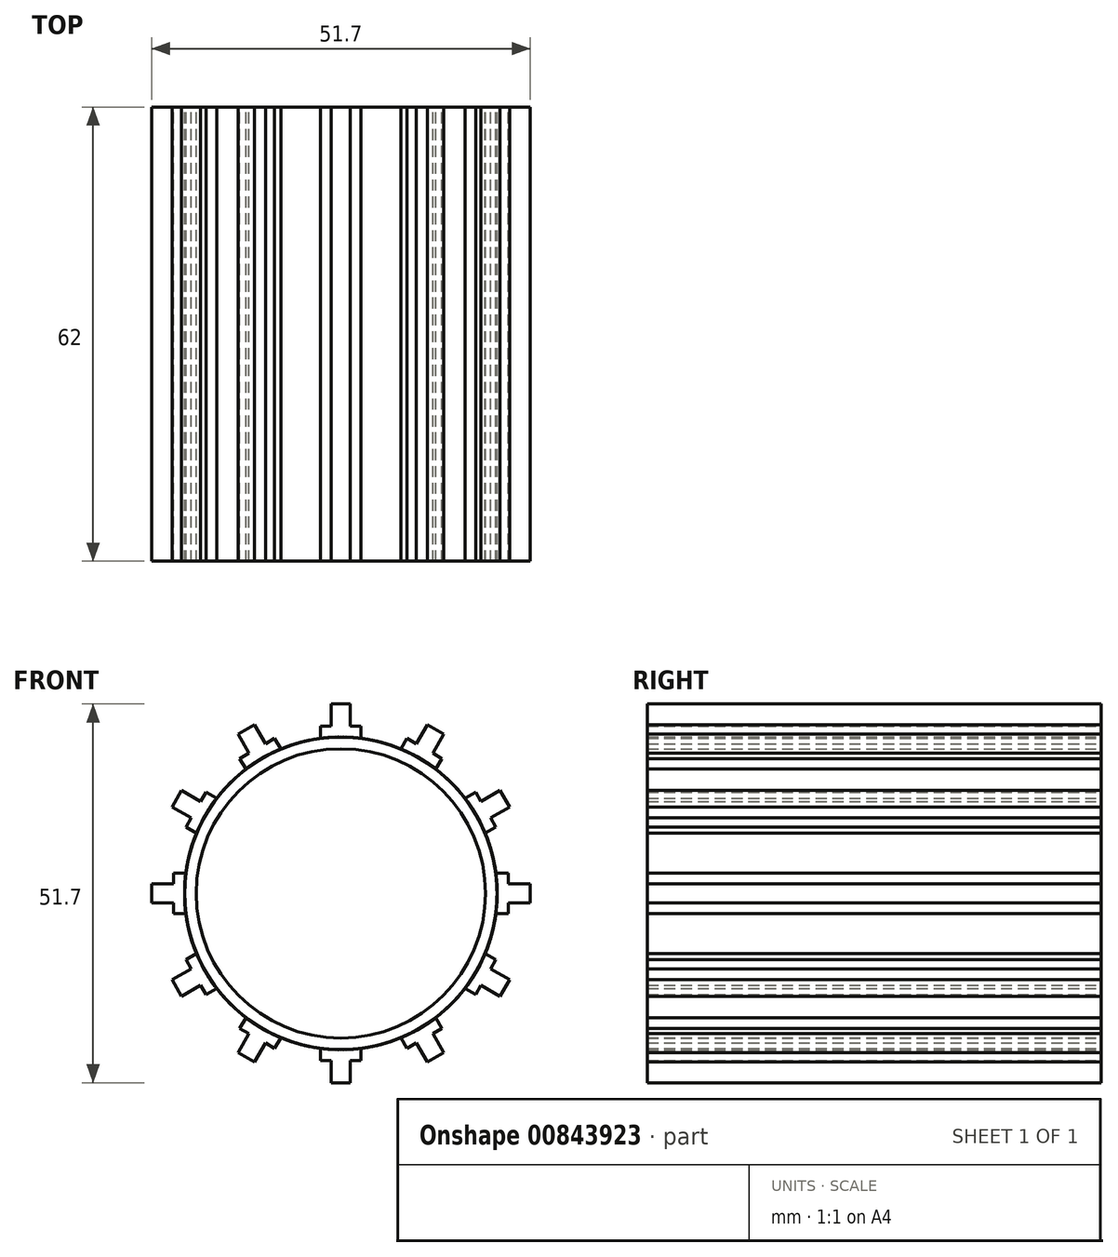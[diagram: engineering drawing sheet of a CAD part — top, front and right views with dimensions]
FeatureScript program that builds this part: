
annotation { "Feature Type Name" : "Feature", "Feature Type Description" : "" }
export const myFeature = defineFeature(function(context is Context, id is Id, definition is map)
    precondition{}
    {
        {
            var Q0;
            Q0=qCreatedBy(makeId("Front.planeOp"),FACE);
            var sketch = newSketch(context, id + "F0", { "sketchPlane" : qUnion([Q0])});
            skCircle(sketch, "E0", {"center": v(0, 0) * mm, "radius": 19.75 * mm});
            skCircle(sketch, "E1.0", {"center": v(0, 0) * mm, "radius": 21.35 * mm});
            skSolve(sketch);
        }
        {
            var Q0;
            Q0=makeQuery(id+"F0.imprint","IMPRINT",FACE,{"disambiguationData":[TD([[makeQuery(id+"F0.imprint","IMPRINT",EDGE,{"derivedFrom":sQuery(id+"F0.wireOp",EDGE,"E0")}),-1.0]])]});
            extrude(context, id + "F1", {"entities" : qUnion([Q0]), "depth" : 62 * mm, "offsetDistance" : 25 * mm});
        }
        {
            var Q0;
            Q0=makeQuery(id+"F1.opExtrude","CAP_FACE",FACE,{"disambiguationData":[OSD([sQuery(id+"F0.wireOp",EDGE,"E0"),sQuery(id+"F0.wireOp",EDGE,"E1.0")])],"isStart":true});
            var sketch = newSketch(context, id + "F2", { "sketchPlane" : qUnion([Q0])});
            skLineSegment(sketch, "E2", {"start": v(-2.75, 21.17) * mm, "end": v(-2.75, 22.85) * mm});
            skLineSegment(sketch, "E3", {"start": v(2.75, 22.85) * mm, "end": v(2.75, 21.17) * mm});
            skLineSegment(sketch, "E4", {"start": v(-1.3, 22.85) * mm, "end": v(-1.3, 25.85) * mm});
            skLineSegment(sketch, "E5", {"start": v(-2.75, 22.85) * mm, "end": v(-1.3, 22.85) * mm});
            skLineSegment(sketch, "E6", {"start": v(-1.3, 25.85) * mm, "end": v(1.3, 25.85) * mm});
            skLineSegment(sketch, "E7", {"start": v(1.3, 25.85) * mm, "end": v(1.3, 22.85) * mm});
            skLineSegment(sketch, "E8", {"start": v(1.3, 22.85) * mm, "end": v(2.75, 22.85) * mm});
            skSolve(sketch);
        }
        {
            var Q0;
            {var subQ0=sQuery(id+"F2.wireOp",EDGE,"E4");Q0=makeQuery(id+"F2.imprint","IMPRINT",FACE,{"disambiguationData":[TD([[makeQuery(id+"F2.imprint","IMPRINT",EDGE,{"derivedFrom":subQ0}),-1.0]])]});}
            var Q1;
            {var subQ4=sQuery(id+"F2.wireOp",EDGE,"E2");Q1=makeQuery(id+"F2.imprint","IMPRINT",FACE,{"disambiguationData":[TD([[makeQuery(id+"F2.imprint","IMPRINT",EDGE,{"derivedFrom":subQ4}),-1.0]])]});}
            extrude(context, id + "F3", {"entities" : qUnion([Q0, Q1]), "operationType" : NewBodyOperationType.ADD, "depth" : -62 * mm, "offsetDistance" : 25 * mm});
        }
        {
            var Q0;
            Q0=makeQuery(id+"F1.opExtrude","SWEPT_BODY",BODY,{"disambiguationData":[OSD([sQuery(id+"F0.wireOp",EDGE,"E0"),sQuery(id+"F0.wireOp",EDGE,"E1.0")])]});
            var Q1;
            Q1=makeQuery(id+"F1.opExtrude","SWEPT_FACE",FACE,{"disambiguationData":[OSD([sQuery(id+"F0.wireOp",EDGE,"E0")])]});
            circularPattern(context, id + "F4", {"entities" : qUnion([Q0]), "axis" : qUnion([Q1]), "angle" : 360 * degree, "instanceCount" : 12, "equalSpace" : true});
        }
    });
